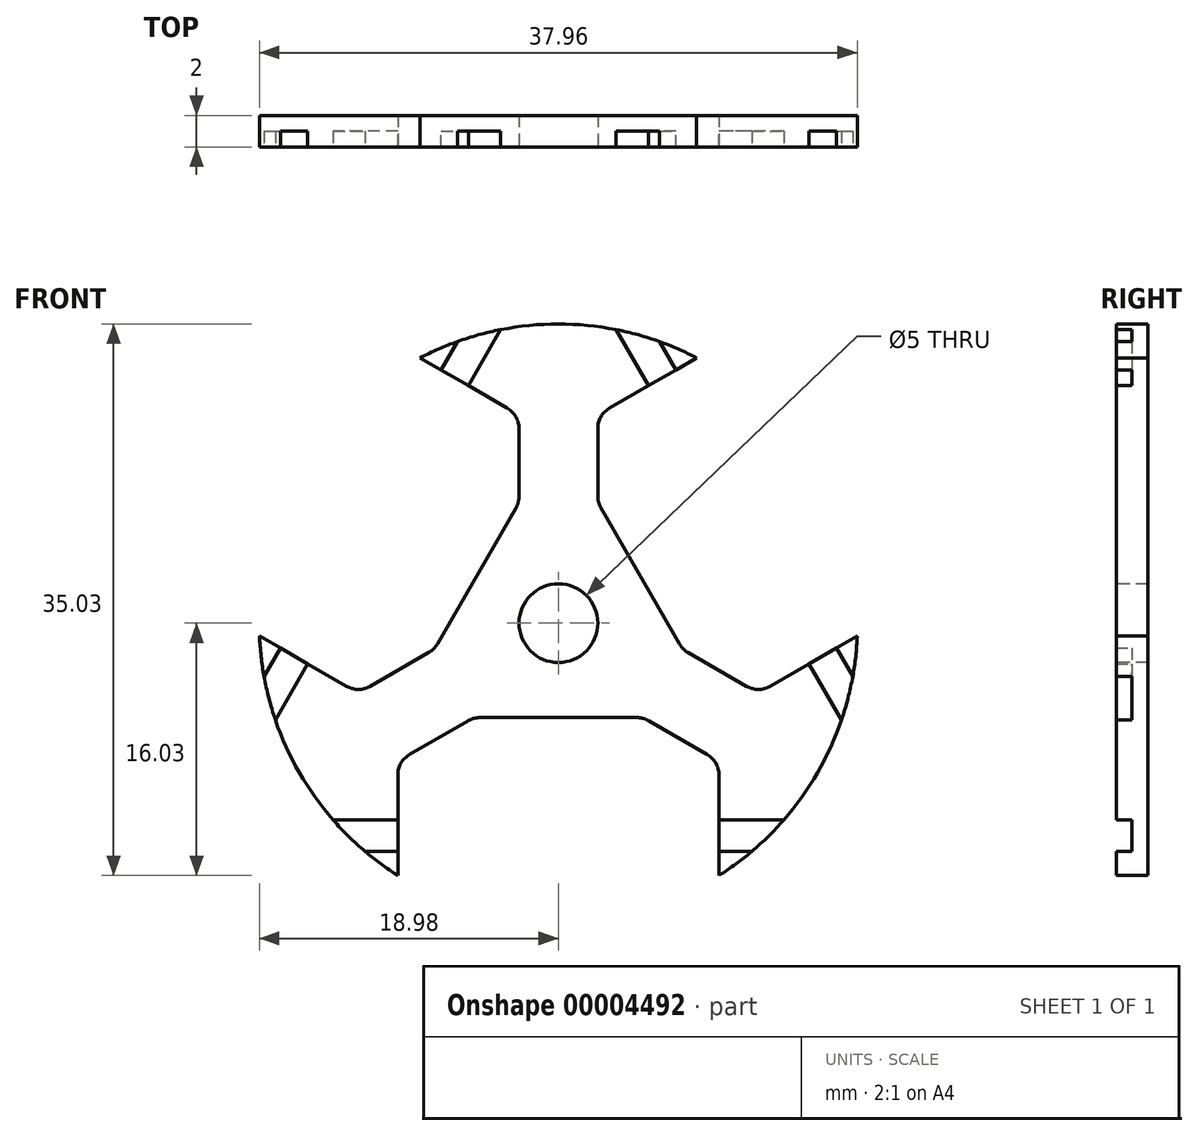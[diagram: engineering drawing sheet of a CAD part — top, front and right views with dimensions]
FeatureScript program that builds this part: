
annotation { "Feature Type Name" : "Feature", "Feature Type Description" : "" }
export const myFeature = defineFeature(function(context is Context, id is Id, definition is map)
    precondition{}
    {
        {
            var Q0;
            Q0=qCreatedBy(makeId("Front.planeOp"),FACE);
            var sketch = newSketch(context, id + "F0", { "sketchPlane" : qUnion([Q0])});
            skCircle(sketch, "E0", {"center": v(0, 0) * mm, "radius": 19 * mm, "construction": true});
            skCircle(sketch, "E1", {"center": v(0, 0) * mm, "radius": 20 * mm, "construction": true});
            skLineSegment(sketch, "E2", {"start": v(0, 0) * mm, "end": v(10, -17.32) * mm, "construction": true});
            skLineSegment(sketch, "E3", {"start": v(10, -17.32) * mm, "end": v(10, -8.66) * mm, "construction": true});
            skLineSegment(sketch, "E4", {"start": v(0, -13.5) * mm, "end": v(14.76, -13.5) * mm, "construction": true});
            skLineSegment(sketch, "E5", {"start": v(10, -12.5) * mm, "end": v(15.61, -12.5) * mm, "construction": true});
            skLineSegment(sketch, "E6", {"start": v(13.77, -14.5) * mm, "end": v(10, -14.5) * mm, "construction": true});
            skLineSegment(sketch, "E7", {"start": v(10.2, -9.64) * mm, "end": v(10.2, -16.03) * mm, "construction": true});
            skCircle(sketch, "E8", {"center": v(0, -27) * mm, "radius": 20 * mm, "construction": true});
            skLineSegment(sketch, "E9", {"start": v(0, -6) * mm, "end": v(5, -6) * mm, "construction": true});
            skLineSegment(sketch, "E10", {"start": v(0, 0) * mm, "end": v(17.32, -10) * mm, "construction": true});
            skLineSegment(sketch, "E11", {"start": v(9.45, -8.34) * mm, "end": v(5.74, -6.2) * mm, "construction": true});
            skLineSegment(sketch, "E12.0.MirrorCS", {"start": v(0, -6) * mm, "end": v(-5, -6) * mm, "construction": true});
            skLineSegment(sketch, "E12.1.MirrorCS", {"start": v(-13.77, -14.5) * mm, "end": v(-10, -14.5) * mm, "construction": true});
            skLineSegment(sketch, "E12.2.MirrorCS", {"start": v(-10, -12.5) * mm, "end": v(-15.61, -12.5) * mm, "construction": true});
            skLineSegment(sketch, "E12.3.MirrorCS", {"start": v(-10.2, -9.64) * mm, "end": v(-10.2, -16.03) * mm, "construction": true});
            skLineSegment(sketch, "E12.4.MirrorCS", {"start": v(0, -13.5) * mm, "end": v(-14.76, -13.5) * mm, "construction": true});
            skLineSegment(sketch, "E12.5.MirrorCS", {"start": v(-10, -17.32) * mm, "end": v(-10, -8.66) * mm, "construction": true});
            skLineSegment(sketch, "E12.6.MirrorCS", {"start": v(-9.45, -8.34) * mm, "end": v(-5.74, -6.2) * mm, "construction": true});
            skLineSegment(sketch, "E13.1.0", {"start": v(11.7, 6.75) * mm, "end": v(4.31, 19.53) * mm, "construction": true});
            skLineSegment(sketch, "E13.1.1", {"start": v(11.7, 6.75) * mm, "end": v(19.07, -6.03) * mm, "construction": true});
            skLineSegment(sketch, "E13.1.2", {"start": v(19.44, -4.68) * mm, "end": v(17.56, -1.41) * mm, "construction": true});
            skLineSegment(sketch, "E13.1.3", {"start": v(3.25, 13.65) * mm, "end": v(8.78, 16.85) * mm, "construction": true});
            skLineSegment(sketch, "E13.1.4", {"start": v(11.95, -4.01) * mm, "end": v(8.24, -1.87) * mm, "construction": true});
            skLineSegment(sketch, "E13.1.5", {"start": v(5.83, 14.91) * mm, "end": v(3.02, 19.77) * mm, "construction": true});
            skLineSegment(sketch, "E13.1.6", {"start": v(13.45, -4.01) * mm, "end": v(18.98, -0.82) * mm, "construction": true});
            skLineSegment(sketch, "E13.1.7", {"start": v(10, 17.32) * mm, "end": v(2.5, 13) * mm, "construction": true});
            skLineSegment(sketch, "E13.1.8", {"start": v(5.2, 3) * mm, "end": v(7.7, -1.32) * mm, "construction": true});
            skLineSegment(sketch, "E13.1.9", {"start": v(15.83, -2.41) * mm, "end": v(18.63, -7.27) * mm, "construction": true});
            skLineSegment(sketch, "E13.1.10", {"start": v(20, 0) * mm, "end": v(12.5, -4.33) * mm, "construction": true});
            skLineSegment(sketch, "E13.1.11", {"start": v(5.2, 3) * mm, "end": v(2.7, 7.32) * mm, "construction": true});
            skLineSegment(sketch, "E13.1.12", {"start": v(5.67, 19.18) * mm, "end": v(7.56, 15.91) * mm, "construction": true});
            skLineSegment(sketch, "E13.1.13", {"start": v(2.5, 12.36) * mm, "end": v(2.5, 8.07) * mm, "construction": true});
            skLineSegment(sketch, "E13.2.0", {"start": v(-11.7, 6.75) * mm, "end": v(-19.07, -6.03) * mm, "construction": true});
            skLineSegment(sketch, "E13.2.1", {"start": v(-11.7, 6.75) * mm, "end": v(-4.31, 19.53) * mm, "construction": true});
            skLineSegment(sketch, "E13.2.2", {"start": v(-5.67, 19.18) * mm, "end": v(-7.56, 15.91) * mm, "construction": true});
            skLineSegment(sketch, "E13.2.3", {"start": v(-13.45, -4.01) * mm, "end": v(-18.98, -0.82) * mm, "construction": true});
            skLineSegment(sketch, "E13.2.4", {"start": v(-2.5, 12.36) * mm, "end": v(-2.5, 8.07) * mm, "construction": true});
            skLineSegment(sketch, "E13.2.5", {"start": v(-15.83, -2.41) * mm, "end": v(-18.63, -7.27) * mm, "construction": true});
            skLineSegment(sketch, "E13.2.6", {"start": v(-3.25, 13.65) * mm, "end": v(-8.78, 16.85) * mm, "construction": true});
            skLineSegment(sketch, "E13.2.7", {"start": v(-20, 0) * mm, "end": v(-12.5, -4.33) * mm, "construction": true});
            skLineSegment(sketch, "E13.2.8", {"start": v(-5.2, 3) * mm, "end": v(-2.7, 7.32) * mm, "construction": true});
            skLineSegment(sketch, "E13.2.9", {"start": v(-5.83, 14.91) * mm, "end": v(-3.02, 19.77) * mm, "construction": true});
            skLineSegment(sketch, "E13.2.10", {"start": v(-10, 17.32) * mm, "end": v(-2.5, 13) * mm, "construction": true});
            skLineSegment(sketch, "E13.2.11", {"start": v(-5.2, 3) * mm, "end": v(-7.7, -1.32) * mm, "construction": true});
            skLineSegment(sketch, "E13.2.12", {"start": v(-19.44, -4.68) * mm, "end": v(-17.56, -1.41) * mm, "construction": true});
            skLineSegment(sketch, "E13.2.13", {"start": v(-11.95, -4.01) * mm, "end": v(-8.24, -1.87) * mm, "construction": true});
            skCircle(sketch, "E14", {"center": v(0, 0) * mm, "radius": 2.5 * mm, "construction": true});
            skPoint(sketch, "E15.visualSharp", {"position": v(5.4, -6) * mm});
            skArc(sketch, "E15.filletArc", {"start": v(5.74, -6.2) * mm, "mid": v(5.38, -6.05) * mm, "end": v(5, -6) * mm, "construction": true});
            skPoint(sketch, "E16.visualSharp", {"position": v(10.2, -8.78) * mm});
            skArc(sketch, "E16.filletArc", {"start": v(10.2, -9.64) * mm, "mid": v(10, -8.9) * mm, "end": v(9.45, -8.34) * mm, "construction": true});
            skPoint(sketch, "E17.visualSharp", {"position": v(-5.4, -6) * mm});
            skArc(sketch, "E17.filletArc", {"start": v(-5, -6) * mm, "mid": v(-5.38, -6.05) * mm, "end": v(-5.74, -6.2) * mm, "construction": true});
            skPoint(sketch, "E18.visualSharp", {"position": v(-10.2, -8.78) * mm});
            skArc(sketch, "E18.filletArc", {"start": v(-9.45, -8.34) * mm, "mid": v(-10, -8.9) * mm, "end": v(-10.2, -9.64) * mm, "construction": true});
            skPoint(sketch, "E19.visualSharp", {"position": v(12.7, -4.45) * mm});
            skArc(sketch, "E19.filletArc", {"start": v(11.95, -4.01) * mm, "mid": v(12.7, -4.21) * mm, "end": v(13.45, -4.01) * mm, "construction": true});
            skPoint(sketch, "E20.visualSharp", {"position": v(7.9, -1.67) * mm});
            skArc(sketch, "E20.filletArc", {"start": v(7.7, -1.32) * mm, "mid": v(7.93, -1.63) * mm, "end": v(8.24, -1.87) * mm, "construction": true});
            skPoint(sketch, "E21.visualSharp", {"position": v(2.5, 7.67) * mm});
            skArc(sketch, "E21.filletArc", {"start": v(2.5, 8.07) * mm, "mid": v(2.55, 7.68) * mm, "end": v(2.7, 7.32) * mm, "construction": true});
            skPoint(sketch, "E22.visualSharp", {"position": v(2.5, 13.22) * mm});
            skArc(sketch, "E22.filletArc", {"start": v(3.25, 13.65) * mm, "mid": v(2.7, 13.1) * mm, "end": v(2.5, 12.36) * mm, "construction": true});
            skPoint(sketch, "E23.visualSharp", {"position": v(-2.5, 13.22) * mm});
            skArc(sketch, "E23.filletArc", {"start": v(-2.5, 12.36) * mm, "mid": v(-2.7, 13.1) * mm, "end": v(-3.25, 13.65) * mm, "construction": true});
            skPoint(sketch, "E24.visualSharp", {"position": v(-2.5, 7.67) * mm});
            skArc(sketch, "E24.filletArc", {"start": v(-2.7, 7.32) * mm, "mid": v(-2.55, 7.68) * mm, "end": v(-2.5, 8.07) * mm, "construction": true});
            skPoint(sketch, "E25.visualSharp", {"position": v(-7.9, -1.67) * mm});
            skArc(sketch, "E25.filletArc", {"start": v(-8.24, -1.87) * mm, "mid": v(-7.93, -1.63) * mm, "end": v(-7.7, -1.32) * mm, "construction": true});
            skPoint(sketch, "E26.visualSharp", {"position": v(-12.7, -4.45) * mm});
            skArc(sketch, "E26.filletArc", {"start": v(-13.45, -4.01) * mm, "mid": v(-12.7, -4.21) * mm, "end": v(-11.95, -4.01) * mm, "construction": true});
            skSolve(sketch);
        }
        {
            var Q0;
            Q0=qCreatedBy(makeId("Front.planeOp"),FACE);
            var sketch = newSketch(context, id + "F1", { "sketchPlane" : qUnion([Q0])});
            skCircle(sketch, "E27.0", {"center": v(0, 0) * mm, "radius": 19 * mm});
            skSolve(sketch);
        }
        {
            var Q0;
            Q0=makeQuery(id+"F1.imprint","IMPRINT",FACE,{"disambiguationData":[TD([[makeQuery(id+"F1.imprint","IMPRINT",EDGE,{"derivedFrom":sQuery(id+"F1.wireOp",EDGE,"E27.0")}),1.0]])]});
            extrude(context, id + "F2", {"entities" : qUnion([Q0]), "oppositeDirection" : true, "depth" : 2 * mm});
        }
        {
            var Q0;
            Q0=qCreatedBy(makeId("Front.planeOp"),FACE);
            var sketch = newSketch(context, id + "F3", { "sketchPlane" : qUnion([Q0])});
            skLineSegment(sketch, "E28.0", {"start": v(-10.2, -9.64) * mm, "end": v(-10.2, -16.03) * mm});
            skLineSegment(sketch, "E28.1", {"start": v(-9.45, -8.34) * mm, "end": v(-5.74, -6.2) * mm});
            skLineSegment(sketch, "E28.2", {"start": v(0, -6) * mm, "end": v(-5, -6) * mm});
            skLineSegment(sketch, "E28.3", {"start": v(0, -6) * mm, "end": v(5, -6) * mm});
            skLineSegment(sketch, "E28.4", {"start": v(9.45, -8.34) * mm, "end": v(5.74, -6.2) * mm});
            skLineSegment(sketch, "E28.5", {"start": v(10.2, -9.64) * mm, "end": v(10.2, -16.03) * mm});
            skLineSegment(sketch, "E28.6", {"start": v(13.45, -4.01) * mm, "end": v(18.98, -0.82) * mm});
            skLineSegment(sketch, "E28.7", {"start": v(11.95, -4.01) * mm, "end": v(8.24, -1.87) * mm});
            skLineSegment(sketch, "E28.8", {"start": v(5.2, 3) * mm, "end": v(7.7, -1.32) * mm});
            skLineSegment(sketch, "E28.9", {"start": v(5.2, 3) * mm, "end": v(2.7, 7.32) * mm});
            skLineSegment(sketch, "E28.10", {"start": v(2.5, 12.36) * mm, "end": v(2.5, 8.07) * mm});
            skLineSegment(sketch, "E28.11", {"start": v(3.25, 13.65) * mm, "end": v(8.78, 16.85) * mm});
            skLineSegment(sketch, "E28.12", {"start": v(-3.25, 13.65) * mm, "end": v(-8.78, 16.85) * mm});
            skLineSegment(sketch, "E28.13", {"start": v(-2.5, 12.36) * mm, "end": v(-2.5, 8.07) * mm});
            skLineSegment(sketch, "E28.14", {"start": v(-5.2, 3) * mm, "end": v(-2.7, 7.32) * mm});
            skLineSegment(sketch, "E28.15", {"start": v(-5.2, 3) * mm, "end": v(-7.7, -1.32) * mm});
            skLineSegment(sketch, "E28.16", {"start": v(-11.95, -4.01) * mm, "end": v(-8.24, -1.87) * mm});
            skLineSegment(sketch, "E28.17", {"start": v(-13.45, -4.01) * mm, "end": v(-18.98, -0.82) * mm});
            skArc(sketch, "E29", {"start": v(-8.78, 16.85) * mm, "mid": v(-16.45, 9.5) * mm, "end": v(-18.98, -0.82) * mm});
            skArc(sketch, "E30", {"start": v(18.98, -0.82) * mm, "mid": v(16.45, 9.5) * mm, "end": v(8.78, 16.85) * mm});
            skArc(sketch, "E31", {"start": v(-10.2, -16.03) * mm, "mid": v(0, -19) * mm, "end": v(10.2, -16.03) * mm});
            skCircle(sketch, "E32.0", {"center": v(0, 0) * mm, "radius": 2.5 * mm});
            skArc(sketch, "E33.0", {"start": v(-13.45, -4.01) * mm, "mid": v(-12.7, -4.21) * mm, "end": v(-11.95, -4.01) * mm});
            skArc(sketch, "E33.1", {"start": v(-8.24, -1.87) * mm, "mid": v(-7.93, -1.63) * mm, "end": v(-7.7, -1.32) * mm});
            skCircle(sketch, "E33.2.0", {"center": v(0, 0) * mm, "radius": 19 * mm});
            skArc(sketch, "E33.3", {"start": v(-2.7, 7.32) * mm, "mid": v(-2.55, 7.68) * mm, "end": v(-2.5, 8.07) * mm});
            skArc(sketch, "E33.4", {"start": v(-2.5, 12.36) * mm, "mid": v(-2.7, 13.1) * mm, "end": v(-3.25, 13.65) * mm});
            skArc(sketch, "E33.5", {"start": v(3.25, 13.65) * mm, "mid": v(2.7, 13.1) * mm, "end": v(2.5, 12.36) * mm});
            skArc(sketch, "E33.6", {"start": v(2.5, 8.07) * mm, "mid": v(2.55, 7.68) * mm, "end": v(2.7, 7.32) * mm});
            skArc(sketch, "E33.7", {"start": v(7.7, -1.32) * mm, "mid": v(7.93, -1.63) * mm, "end": v(8.24, -1.87) * mm});
            skArc(sketch, "E33.8", {"start": v(11.95, -4.01) * mm, "mid": v(12.7, -4.21) * mm, "end": v(13.45, -4.01) * mm});
            skArc(sketch, "E33.9", {"start": v(5.74, -6.2) * mm, "mid": v(5.38, -6.05) * mm, "end": v(5, -6) * mm});
            skArc(sketch, "E33.10", {"start": v(10.2, -9.64) * mm, "mid": v(10, -8.9) * mm, "end": v(9.45, -8.34) * mm});
            skArc(sketch, "E33.11", {"start": v(-5, -6) * mm, "mid": v(-5.38, -6.05) * mm, "end": v(-5.74, -6.2) * mm});
            skArc(sketch, "E33.12", {"start": v(-9.45, -8.34) * mm, "mid": v(-10, -8.9) * mm, "end": v(-10.2, -9.64) * mm});
            skSolve(sketch);
        }
        {
            var Q0;
            Q0=makeQuery(id+"F3.imprint","IMPRINT",FACE,{"disambiguationData":[TD([[makeQuery(id+"F3.imprint","IMPRINT",EDGE,{"derivedFrom":sQuery(id+"F3.wireOp",EDGE,"E28.12")}),1.0]])]});
            var Q1;
            Q1=makeQuery(id+"F3.imprint","IMPRINT",FACE,{"disambiguationData":[TD([[makeQuery(id+"F3.imprint","IMPRINT",EDGE,{"derivedFrom":sQuery(id+"F3.wireOp",EDGE,"E28.6")}),1.0]])]});
            var Q2;
            Q2=makeQuery(id+"F3.imprint","IMPRINT",FACE,{"disambiguationData":[TD([[makeQuery(id+"F3.imprint","IMPRINT",EDGE,{"derivedFrom":sQuery(id+"F3.wireOp",EDGE,"E28.0")}),1.0]])]});
            var Q3;
            Q3=makeQuery(id+"F3.imprint","IMPRINT",FACE,{"disambiguationData":[TD([[makeQuery(id+"F3.imprint","IMPRINT",EDGE,{"derivedFrom":sQuery(id+"F3.wireOp",EDGE,"E32.0")}),1.0]])]});
            extrude(context, id + "F4", {"entities" : qUnion([Q0, Q1, Q2, Q3]), "operationType" : NewBodyOperationType.REMOVE, "endBound" : BoundingType.UP_TO_NEXT, "oppositeDirection" : true, "depth" : 25 * mm});
        }
        {
            var Q0;
            Q0=qCreatedBy(makeId("Right.planeOp"),FACE);
            var sketch = newSketch(context, id + "F5", { "sketchPlane" : qUnion([Q0])});
            skLineSegment(sketch, "E34.rect.bottom", {"start": v(-1, -14.5) * mm, "end": v(1, -14.5) * mm});
            skLineSegment(sketch, "E34.rect.top", {"start": v(-1, -12.5) * mm, "end": v(1, -12.5) * mm});
            skLineSegment(sketch, "E34.rect.left", {"start": v(-1, -14.5) * mm, "end": v(-1, -12.5) * mm});
            skLineSegment(sketch, "E34.rect.right", {"start": v(1, -14.5) * mm, "end": v(1, -12.5) * mm});
            skPoint(sketch, "E34.rect.middle", {"position": v(0, -13.5) * mm});
            skSolve(sketch);
        }
        {
            var Q0;
            Q0=makeQuery(id+"F5.imprint","IMPRINT",FACE,{"disambiguationData":[TD([[makeQuery(id+"F5.imprint","IMPRINT",EDGE,{"derivedFrom":sQuery(id+"F5.wireOp",EDGE,"E34.rect.bottom")}),1.0]])]});
            extrude(context, id + "F6", {"entities" : qUnion([Q0]), "endBound" : BoundingType.SYMMETRIC, "depth" : 40 * mm});
        }
        {
            var Q0;
            Q0=qCreatedBy(makeId("Top.planeOp"),FACE);
            var sketch = newSketch(context, id + "F7", { "sketchPlane" : qUnion([Q0])});
            skLineSegment(sketch, "E35", {"start": v(0, 0) * mm, "end": v(0, 2) * mm, "construction": true});
            skSolve(sketch);
        }
        {
            var Q0;
            Q0=makeQuery(id+"F6.opExtrude","SWEPT_BODY",BODY,{"disambiguationData":[OSD([sQuery(id+"F5.wireOp",EDGE,"E34.rect.bottom"),sQuery(id+"F5.wireOp",EDGE,"E34.rect.top"),sQuery(id+"F5.wireOp",EDGE,"E34.rect.left"),sQuery(id+"F5.wireOp",EDGE,"E34.rect.right")])]});
            var Q1;
            Q1=sQuery(id+"F7.wireOp",EDGE,"E35");
            circularPattern(context, id + "F8", {"entities" : qUnion([Q0]), "axis" : qUnion([Q1]), "angle" : 120 * degree, "instanceCount" : 3});
        }
        {
            var Q0;
            Q0=makeQuery(id+"F8.opPattern","COPY",BODY,{"derivedFrom":makeQuery(id+"F6.opExtrude","SWEPT_BODY",BODY,{"disambiguationData":[OSD([sQuery(id+"F5.wireOp",EDGE,"E34.rect.bottom"),sQuery(id+"F5.wireOp",EDGE,"E34.rect.top"),sQuery(id+"F5.wireOp",EDGE,"E34.rect.left"),sQuery(id+"F5.wireOp",EDGE,"E34.rect.right")])]}),"instanceName":"1"});
            var Q1;
            Q1=makeQuery(id+"F8.opPattern","COPY",BODY,{"derivedFrom":makeQuery(id+"F6.opExtrude","SWEPT_BODY",BODY,{"disambiguationData":[OSD([sQuery(id+"F5.wireOp",EDGE,"E34.rect.bottom"),sQuery(id+"F5.wireOp",EDGE,"E34.rect.top"),sQuery(id+"F5.wireOp",EDGE,"E34.rect.left"),sQuery(id+"F5.wireOp",EDGE,"E34.rect.right")])]}),"instanceName":"2"});
            var Q2;
            Q2=makeQuery(id+"F6.opExtrude","SWEPT_BODY",BODY,{"disambiguationData":[OSD([sQuery(id+"F5.wireOp",EDGE,"E34.rect.bottom"),sQuery(id+"F5.wireOp",EDGE,"E34.rect.top"),sQuery(id+"F5.wireOp",EDGE,"E34.rect.left"),sQuery(id+"F5.wireOp",EDGE,"E34.rect.right")])]});
            var Q3;
            Q3=makeQuery(id+"F2.opExtrude","SWEPT_BODY",BODY,{"disambiguationData":[OSD([sQuery(id+"F1.wireOp",EDGE,"E27.0")])]});
            booleanBodies(context, id + "F9", {"operationType" : BooleanOperationType.SUBTRACTION, "tools" : qUnion([Q0, Q1, Q2]), "targets" : qUnion([Q3])});
        }
    });
